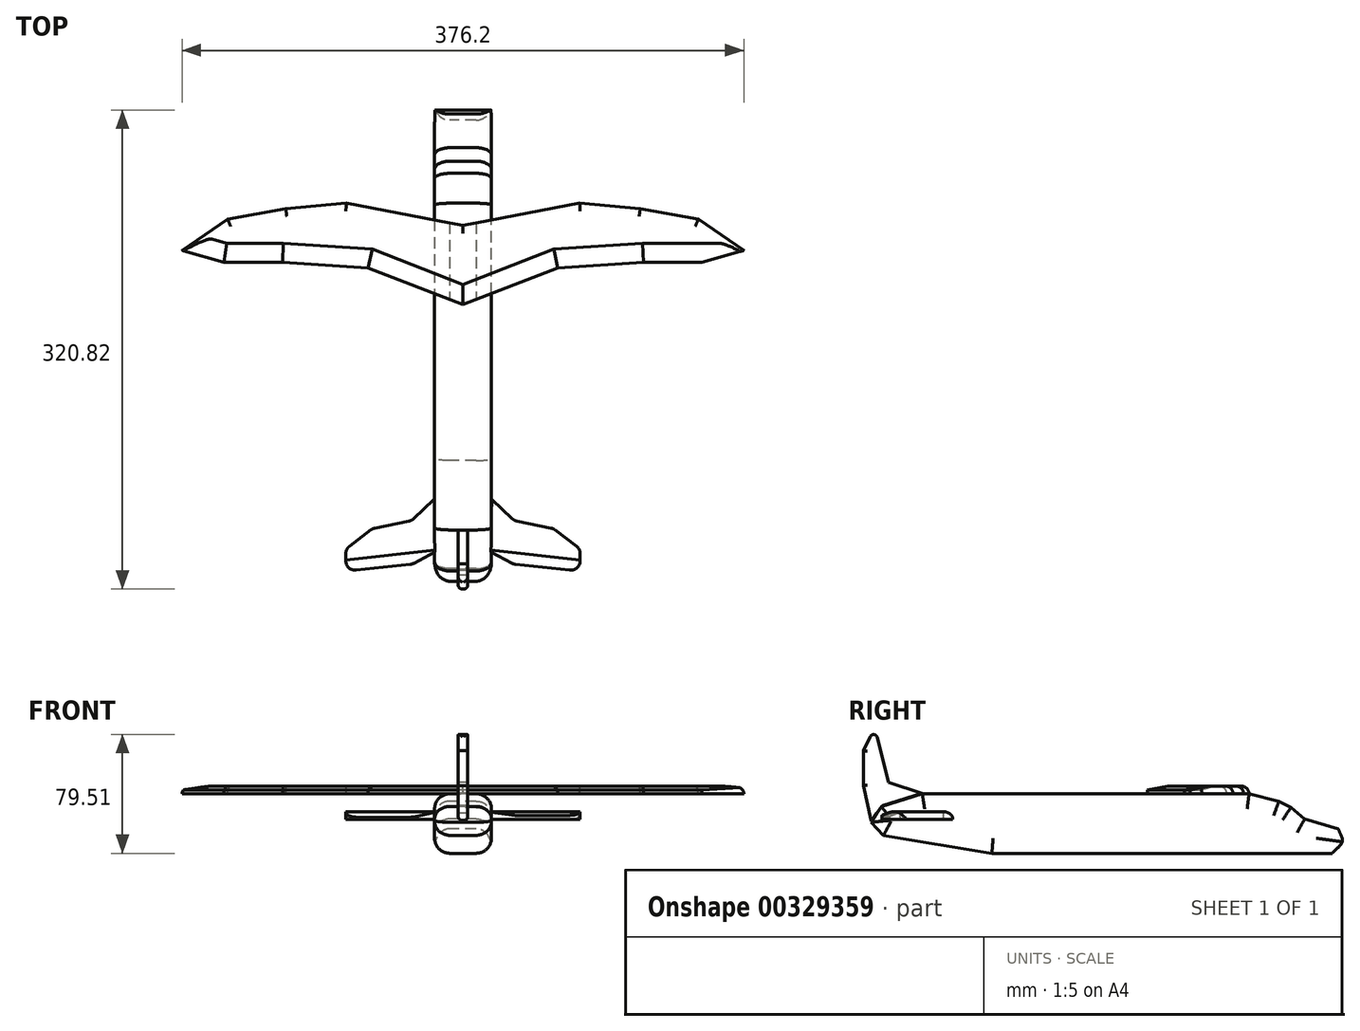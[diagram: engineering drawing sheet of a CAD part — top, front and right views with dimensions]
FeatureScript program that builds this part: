
annotation { "Feature Type Name" : "Feature", "Feature Type Description" : "" }
export const myFeature = defineFeature(function(context is Context, id is Id, definition is map)
    precondition{}
    {
        {
            var Q0;
            Q0=qCreatedBy(makeId("Right.planeOp"),FACE);
            var sketch = newSketch(context, id + "F0", { "sketchPlane" : qUnion([Q0])});
            skLineSegment(sketch, "E0", {"start": v(-78.46, 0) * mm, "end": v(149.41, 0) * mm});
            skLineSegment(sketch, "E1", {"start": v(149.41, 0) * mm, "end": v(157.23, 7.66) * mm});
            skLineSegment(sketch, "E2", {"start": v(157.23, 7.66) * mm, "end": v(153.48, 16.41) * mm});
            skLineSegment(sketch, "E3", {"start": v(153.48, 16.41) * mm, "end": v(130.97, 22.97) * mm});
            skLineSegment(sketch, "E4", {"start": v(130.97, 22.97) * mm, "end": v(121.9, 30.79) * mm});
            skLineSegment(sketch, "E5", {"start": v(121.9, 30.79) * mm, "end": v(113.78, 34.85) * mm});
            skLineSegment(sketch, "E6", {"start": v(113.78, 34.85) * mm, "end": v(93.77, 39.85) * mm});
            skLineSegment(sketch, "E7", {"start": v(93.77, 39.85) * mm, "end": v(-34.7, 39.85) * mm});
            skLineSegment(sketch, "E8", {"start": v(-34.7, 39.85) * mm, "end": v(-125.03, 39.85) * mm});
            skLineSegment(sketch, "E9", {"start": v(-125.03, 39.85) * mm, "end": v(-152.54, 31.41) * mm});
            skLineSegment(sketch, "E10", {"start": v(-152.54, 31.41) * mm, "end": v(-159.42, 20.79) * mm});
            skLineSegment(sketch, "E11", {"start": v(-159.42, 20.79) * mm, "end": v(-150.98, 12.03) * mm});
            skLineSegment(sketch, "E12", {"start": v(-150.98, 12.03) * mm, "end": v(-78.46, 0) * mm});
            skSolve(sketch);
        }
        {
            var Q0;
            Q0=qSketchRegion(id+"F0",true);
            extrude(context, id + "F1", {"entities" : qUnion([Q0]), "endBound" : BoundingType.SYMMETRIC, "depth" : 38.1 * mm});
        }
        {
            var Q0;
            Q0=makeQuery(id+"F1.opExtrude","CAP_FACE",FACE,{"disambiguationData":[OSD([sQuery(id+"F0.wireOp",EDGE,"E0"),sQuery(id+"F0.wireOp",EDGE,"E1"),sQuery(id+"F0.wireOp",EDGE,"E2"),sQuery(id+"F0.wireOp",EDGE,"E3"),sQuery(id+"F0.wireOp",EDGE,"E4"),sQuery(id+"F0.wireOp",EDGE,"E5"),sQuery(id+"F0.wireOp",EDGE,"E6"),sQuery(id+"F0.wireOp",EDGE,"E7"),sQuery(id+"F0.wireOp",EDGE,"E8"),sQuery(id+"F0.wireOp",EDGE,"E9"),sQuery(id+"F0.wireOp",EDGE,"E10"),sQuery(id+"F0.wireOp",EDGE,"E11"),sQuery(id+"F0.wireOp",EDGE,"E12")])],"isStart":false});
            var Q1;
            Q1=makeQuery(id+"F1.opExtrude","CAP_FACE",FACE,{"disambiguationData":[OSD([sQuery(id+"F0.wireOp",EDGE,"E0"),sQuery(id+"F0.wireOp",EDGE,"E1"),sQuery(id+"F0.wireOp",EDGE,"E2"),sQuery(id+"F0.wireOp",EDGE,"E3"),sQuery(id+"F0.wireOp",EDGE,"E4"),sQuery(id+"F0.wireOp",EDGE,"E5"),sQuery(id+"F0.wireOp",EDGE,"E6"),sQuery(id+"F0.wireOp",EDGE,"E7"),sQuery(id+"F0.wireOp",EDGE,"E8"),sQuery(id+"F0.wireOp",EDGE,"E9"),sQuery(id+"F0.wireOp",EDGE,"E10"),sQuery(id+"F0.wireOp",EDGE,"E11"),sQuery(id+"F0.wireOp",EDGE,"E12")])],"isStart":true});
            fillet(context, id + "F2", {"entities" : qUnion([Q0, Q1]), "radius" : 10.16 * mm, "tangentPropagation" : true, "allowEdgeOverflow" : false});
        }
        {
            var Q0;
            Q0=makeQuery(id+"F1.opExtrude","SWEPT_EDGE",EDGE,{"disambiguationData":[OSD([sQuery(id+"F0.wireOp",EDGE,"E1"),sQuery(id+"F0.wireOp",EDGE,"E2")])]});
            fillet(context, id + "F3", {"entities" : qUnion([Q0]), "radius" : 5.08 * mm, "tangentPropagation" : true, "allowEdgeOverflow" : false});
        }
        {
            var Q0;
            Q0=makeQuery(id+"F1.opExtrude","SWEPT_FACE",FACE,{"disambiguationData":[OSD([sQuery(id+"F0.wireOp",EDGE,"E7"),sQuery(id+"F0.wireOp",EDGE,"E8")])]});
            var sketch = newSketch(context, id + "F4", { "sketchPlane" : qUnion([Q0])});
            skLineSegment(sketch, "E13", {"start": v(0, 78.89) * mm, "end": v(-78.16, 93.77) * mm});
            skLineSegment(sketch, "E14", {"start": v(-78.16, 93.77) * mm, "end": v(-118.71, 90.18) * mm});
            skLineSegment(sketch, "E15", {"start": v(-118.71, 90.18) * mm, "end": v(-157.58, 83.07) * mm});
            skLineSegment(sketch, "E16", {"start": v(-157.58, 83.07) * mm, "end": v(-188.1, 62.17) * mm});
            skLineSegment(sketch, "E17", {"start": v(-188.1, 62.17) * mm, "end": v(-160.1, 54.23) * mm});
            skLineSegment(sketch, "E18", {"start": v(-160.1, 54.23) * mm, "end": v(-120.8, 54.23) * mm});
            skLineSegment(sketch, "E19", {"start": v(-120.8, 54.23) * mm, "end": v(-63.54, 50.47) * mm});
            skLineSegment(sketch, "E20", {"start": v(-63.54, 50.47) * mm, "end": v(0, 25.8) * mm});
            skLineSegment(sketch, "E21", {"start": v(0, 0) * mm, "end": v(0, 154.96) * mm, "construction": true});
            skLineSegment(sketch, "E22.0.MirrorCS", {"start": v(78.16, 93.77) * mm, "end": v(118.71, 90.18) * mm});
            skLineSegment(sketch, "E22.1.MirrorCS", {"start": v(118.71, 90.18) * mm, "end": v(157.58, 83.07) * mm});
            skLineSegment(sketch, "E22.2.MirrorCS", {"start": v(63.54, 50.47) * mm, "end": v(0, 25.8) * mm});
            skLineSegment(sketch, "E22.3.MirrorCS", {"start": v(157.58, 83.07) * mm, "end": v(188.1, 62.17) * mm});
            skLineSegment(sketch, "E22.4.MirrorCS", {"start": v(188.1, 62.17) * mm, "end": v(160.1, 54.23) * mm});
            skLineSegment(sketch, "E22.5.MirrorCS", {"start": v(160.1, 54.23) * mm, "end": v(120.8, 54.23) * mm});
            skLineSegment(sketch, "E22.6.MirrorCS", {"start": v(0, 78.89) * mm, "end": v(78.16, 93.77) * mm});
            skLineSegment(sketch, "E22.7.MirrorCS", {"start": v(120.8, 54.23) * mm, "end": v(63.54, 50.47) * mm});
            skSolve(sketch);
        }
        {
            var Q0;
            Q0=qSketchRegion(id+"F4",true);
            extrude(context, id + "F5", {"entities" : qUnion([Q0]), "operationType" : NewBodyOperationType.ADD, "depth" : 5.08 * mm});
        }
        {
            var Q0;
            Q0=qCreatedBy(makeId("Right.planeOp"),FACE);
            var sketch = newSketch(context, id + "F6", { "sketchPlane" : qUnion([Q0])});
            skLineSegment(sketch, "E23", {"start": v(-159.33, 21.94) * mm, "end": v(-164.55, 45.27) * mm});
            skLineSegment(sketch, "E24", {"start": v(-164.55, 45.27) * mm, "end": v(-164.55, 68.9) * mm});
            skLineSegment(sketch, "E25", {"start": v(-164.55, 68.9) * mm, "end": v(-156.87, 84.25) * mm});
            skLineSegment(sketch, "E26", {"start": v(-156.87, 84.25) * mm, "end": v(-147.67, 47.42) * mm});
            skLineSegment(sketch, "E27", {"start": v(-147.67, 47.42) * mm, "end": v(-125.26, 40.05) * mm});
            skLineSegment(sketch, "E28", {"start": v(-125.26, 40.05) * mm, "end": v(-151.66, 31.77) * mm});
            skLineSegment(sketch, "E29", {"start": v(-151.66, 31.77) * mm, "end": v(-159.33, 21.94) * mm});
            skSolve(sketch);
        }
        {
            var Q0;
            Q0=makeQuery(id+"F6.imprint","IMPRINT",FACE,{"disambiguationData":[TD([[makeQuery(id+"F6.imprint","IMPRINT",EDGE,{"derivedFrom":sQuery(id+"F6.wireOp",EDGE,"E23")}),-1.0]])]});
            extrude(context, id + "F7", {"entities" : qUnion([Q0]), "operationType" : NewBodyOperationType.ADD, "endBound" : BoundingType.SYMMETRIC, "depth" : 6.35 * mm});
        }
        {
            var Q0;
            Q0=makeQuery(id+"F7.opExtrude","CAP_EDGE",EDGE,{"disambiguationData":[OSD([sQuery(id+"F6.wireOp",EDGE,"E25")])],"isStart":false});
            var Q1;
            Q1=makeQuery(id+"F7.opExtrude","CAP_EDGE",EDGE,{"disambiguationData":[OSD([sQuery(id+"F6.wireOp",EDGE,"E24")])],"isStart":false});
            var Q2;
            Q2=makeQuery(id+"F7.opExtrude","CAP_EDGE",EDGE,{"disambiguationData":[OSD([sQuery(id+"F6.wireOp",EDGE,"E23")])],"isStart":false});
            var Q3;
            Q3=makeQuery(id+"F7.opExtrude","CAP_EDGE",EDGE,{"disambiguationData":[OSD([sQuery(id+"F6.wireOp",EDGE,"E23")])],"isStart":true});
            var Q4;
            Q4=makeQuery(id+"F7.opExtrude","CAP_EDGE",EDGE,{"disambiguationData":[OSD([sQuery(id+"F6.wireOp",EDGE,"E24")])],"isStart":true});
            var Q5;
            Q5=makeQuery(id+"F7.opExtrude","CAP_EDGE",EDGE,{"disambiguationData":[OSD([sQuery(id+"F6.wireOp",EDGE,"E25")])],"isStart":true});
            var Q6;
            Q6=makeQuery(id+"F7.opExtrude","SWEPT_EDGE",EDGE,{"disambiguationData":[OSD([sQuery(id+"F6.wireOp",EDGE,"E25"),sQuery(id+"F6.wireOp",EDGE,"E26")])]});
            fillet(context, id + "F8", {"entities" : qUnion([Q0, Q1, Q2, Q3, Q4, Q5, Q6]), "radius" : 2.54 * mm, "tangentPropagation" : true, "allowEdgeOverflow" : false});
        }
        {
            var Q0;
            Q0=qCreatedBy(makeId("Top.planeOp"),FACE);
            cPlane(context, id + "F9", {"entities" : qUnion([Q0]), "cplaneType" : CPlaneType.OFFSET, "offset" : 25.4 * mm, "width" : 152.4 * mm, "height" : 152.4 * mm});
        }
        {
            var Q0;
            Q0=qCreatedBy(id+"F9.planeOp",FACE);
            var sketch = newSketch(context, id + "F10", { "sketchPlane" : qUnion([Q0])});
            skLineSegment(sketch, "E30", {"start": v(19.38, -104.66) * mm, "end": v(33.06, -117.54) * mm});
            skLineSegment(sketch, "E31", {"start": v(36.15, -119.14) * mm, "end": v(58.99, -123.79) * mm});
            skLineSegment(sketch, "E32", {"start": v(61.55, -124.94) * mm, "end": v(75.97, -135.84) * mm});
            skLineSegment(sketch, "E33", {"start": v(78.49, -140.9) * mm, "end": v(78.49, -145.67) * mm});
            skLineSegment(sketch, "E34", {"start": v(71.45, -151.98) * mm, "end": v(35.17, -148.03) * mm});
            skLineSegment(sketch, "E35", {"start": v(32.84, -147.3) * mm, "end": v(17.61, -139.07) * mm});
            skLineSegment(sketch, "E36", {"start": v(19.38, -104.66) * mm, "end": v(17.61, -139.07) * mm});
            skPoint(sketch, "E37.visualSharp", {"position": v(78.49, -137.75) * mm});
            skArc(sketch, "E37.filletArc", {"start": v(78.49, -140.9) * mm, "mid": v(77.82, -138.08) * mm, "end": v(75.97, -135.84) * mm});
            skPoint(sketch, "E38.visualSharp", {"position": v(78.49, -152.74) * mm});
            skArc(sketch, "E38.filletArc", {"start": v(71.45, -151.98) * mm, "mid": v(76.38, -150.4) * mm, "end": v(78.49, -145.67) * mm});
            skPoint(sketch, "E39.visualSharp", {"position": v(60.4, -124.07) * mm});
            skArc(sketch, "E39.filletArc", {"start": v(61.55, -124.94) * mm, "mid": v(60.33, -124.22) * mm, "end": v(58.99, -123.79) * mm});
            skPoint(sketch, "E40.visualSharp", {"position": v(34.38, -118.78) * mm});
            skArc(sketch, "E40.filletArc", {"start": v(33.06, -117.54) * mm, "mid": v(34.5, -118.56) * mm, "end": v(36.15, -119.14) * mm});
            skPoint(sketch, "E41.visualSharp", {"position": v(33.93, -147.9) * mm});
            skArc(sketch, "E41.filletArc", {"start": v(32.84, -147.3) * mm, "mid": v(33.97, -147.78) * mm, "end": v(35.17, -148.03) * mm});
            skLineSegment(sketch, "E42", {"start": v(0, 0) * mm, "end": v(0, -233.9) * mm, "construction": true});
            skLineSegment(sketch, "E43.0.MirrorCS", {"start": v(-71.45, -151.98) * mm, "end": v(-35.17, -148.03) * mm});
            skLineSegment(sketch, "E44.0.MirrorCS", {"start": v(-78.49, -140.9) * mm, "end": v(-78.49, -145.67) * mm});
            skArc(sketch, "E44.1.MirrorCS", {"start": v(-78.49, -140.9) * mm, "mid": v(-77.82, -138.08) * mm, "end": v(-75.97, -135.84) * mm});
            skArc(sketch, "E44.2.MirrorCS", {"start": v(-61.55, -124.94) * mm, "mid": v(-60.33, -124.22) * mm, "end": v(-58.99, -123.79) * mm});
            skArc(sketch, "E44.3.MirrorCS", {"start": v(-32.84, -147.3) * mm, "mid": v(-33.97, -147.78) * mm, "end": v(-35.17, -148.03) * mm});
            skArc(sketch, "E44.4.MirrorCS", {"start": v(-33.06, -117.54) * mm, "mid": v(-34.5, -118.56) * mm, "end": v(-36.15, -119.14) * mm});
            skArc(sketch, "E44.5.MirrorCS", {"start": v(-71.45, -151.98) * mm, "mid": v(-76.38, -150.4) * mm, "end": v(-78.49, -145.67) * mm});
            skLineSegment(sketch, "E44.7.MirrorCS", {"start": v(-19.38, -104.66) * mm, "end": v(-17.61, -139.07) * mm});
            skPoint(sketch, "E44.8.MirrorP", {"position": v(-60.4, -124.07) * mm});
            skPoint(sketch, "E44.9.MirrorP", {"position": v(-78.49, -137.75) * mm});
            skLineSegment(sketch, "E44.10.MirrorCS", {"start": v(-32.84, -147.3) * mm, "end": v(-17.61, -139.07) * mm});
            skPoint(sketch, "E44.11.MirrorP", {"position": v(-33.93, -147.9) * mm});
            skPoint(sketch, "E44.12.MirrorP", {"position": v(-78.49, -152.74) * mm});
            skLineSegment(sketch, "E44.13.MirrorCS", {"start": v(-61.55, -124.94) * mm, "end": v(-75.97, -135.84) * mm});
            skPoint(sketch, "E44.14.MirrorP", {"position": v(-34.38, -118.78) * mm});
            skLineSegment(sketch, "E44.15.MirrorCS", {"start": v(-19.38, -104.66) * mm, "end": v(-33.06, -117.54) * mm});
            skLineSegment(sketch, "E44.16.MirrorCS", {"start": v(-36.15, -119.14) * mm, "end": v(-58.99, -123.79) * mm});
            skSolve(sketch);
        }
        {
            var Q0;
            Q0=makeQuery(id+"F10.imprint","IMPRINT",FACE,{"disambiguationData":[TD([[makeQuery(id+"F10.imprint","IMPRINT",EDGE,{"derivedFrom":sQuery(id+"F10.wireOp",EDGE,"E30")}),-1.0]])]});
            var Q1;
            Q1=makeQuery(id+"F10.imprint","IMPRINT",FACE,{"disambiguationData":[TD([[makeQuery(id+"F10.imprint","IMPRINT",EDGE,{"derivedFrom":sQuery(id+"F10.wireOp",EDGE,"E44.0.MirrorCS")}),1.0]])]});
            extrude(context, id + "F11", {"entities" : qUnion([Q0, Q1]), "operationType" : NewBodyOperationType.ADD, "endBound" : BoundingType.SYMMETRIC, "depth" : 5.08 * mm});
        }
        {
            var Q0;
            Q0=makeQuery(id+"F5.opExtrude","CAP_EDGE",EDGE,{"disambiguationData":[OSD([sQuery(id+"F4.wireOp",EDGE,"E13")])],"isStart":false});
            var Q1;
            Q1=makeQuery(id+"F5.opExtrude","CAP_EDGE",EDGE,{"disambiguationData":[OSD([sQuery(id+"F4.wireOp",EDGE,"E22.6.MirrorCS")])],"isStart":false});
            var Q2;
            Q2=makeQuery(id+"F5.opExtrude","CAP_EDGE",EDGE,{"disambiguationData":[OSD([sQuery(id+"F4.wireOp",EDGE,"E22.1.MirrorCS")])],"isStart":false});
            var Q3;
            Q3=makeQuery(id+"F5.opExtrude","CAP_EDGE",EDGE,{"disambiguationData":[OSD([sQuery(id+"F4.wireOp",EDGE,"E22.0.MirrorCS")])],"isStart":false});
            var Q4;
            Q4=makeQuery(id+"F5.opExtrude","CAP_EDGE",EDGE,{"disambiguationData":[OSD([sQuery(id+"F4.wireOp",EDGE,"E14")])],"isStart":false});
            var Q5;
            Q5=makeQuery(id+"F5.opExtrude","CAP_EDGE",EDGE,{"disambiguationData":[OSD([sQuery(id+"F4.wireOp",EDGE,"E15")])],"isStart":false});
            var Q6;
            Q6=makeQuery(id+"F5.opExtrude","CAP_EDGE",EDGE,{"disambiguationData":[OSD([sQuery(id+"F4.wireOp",EDGE,"E16")])],"isStart":false});
            var Q7;
            Q7=makeQuery(id+"F5.opExtrude","CAP_EDGE",EDGE,{"disambiguationData":[OSD([sQuery(id+"F4.wireOp",EDGE,"E22.3.MirrorCS")])],"isStart":false});
            var Q8;
            Q8=makeQuery(id+"F11.opExtrude","CAP_EDGE",EDGE,{"disambiguationData":[OSD([sQuery(id+"F10.wireOp",EDGE,"E30")])],"isStart":false});
            var Q9;
            Q9=makeQuery(id+"F11.opExtrude","CAP_EDGE",EDGE,{"disambiguationData":[OSD([sQuery(id+"F10.wireOp",EDGE,"E44.15.MirrorCS")])],"isStart":false});
            var Q10;
            Q10=makeQuery(id+"F11.opExtrude","CAP_EDGE",EDGE,{"disambiguationData":[OSD([sQuery(id+"F10.wireOp",EDGE,"E40.filletArc")])],"isStart":false});
            var Q11;
            Q11=makeQuery(id+"F11.opExtrude","CAP_EDGE",EDGE,{"disambiguationData":[OSD([sQuery(id+"F10.wireOp",EDGE,"E31")])],"isStart":false});
            var Q12;
            Q12=makeQuery(id+"F11.opExtrude","CAP_EDGE",EDGE,{"disambiguationData":[OSD([sQuery(id+"F10.wireOp",EDGE,"E39.filletArc")])],"isStart":false});
            var Q13;
            Q13=makeQuery(id+"F11.opExtrude","CAP_EDGE",EDGE,{"disambiguationData":[OSD([sQuery(id+"F10.wireOp",EDGE,"E32")])],"isStart":false});
            var Q14;
            Q14=makeQuery(id+"F11.opExtrude","CAP_EDGE",EDGE,{"disambiguationData":[OSD([sQuery(id+"F10.wireOp",EDGE,"E37.filletArc")])],"isStart":false});
            var Q15;
            Q15=makeQuery(id+"F11.opExtrude","CAP_EDGE",EDGE,{"disambiguationData":[OSD([sQuery(id+"F10.wireOp",EDGE,"E44.4.MirrorCS")])],"isStart":false});
            var Q16;
            Q16=makeQuery(id+"F11.opExtrude","CAP_EDGE",EDGE,{"disambiguationData":[OSD([sQuery(id+"F10.wireOp",EDGE,"E44.16.MirrorCS")])],"isStart":false});
            var Q17;
            Q17=makeQuery(id+"F11.opExtrude","SWEPT_EDGE",EDGE,{"disambiguationData":[OSD([sQuery(id+"F10.wireOp",EDGE,"E44.2.MirrorCS"),sQuery(id+"F10.wireOp",EDGE,"E44.13.MirrorCS")])]});
            var Q18;
            Q18=makeQuery(id+"F11.opExtrude","CAP_EDGE",EDGE,{"disambiguationData":[OSD([sQuery(id+"F10.wireOp",EDGE,"E44.13.MirrorCS")])],"isStart":false});
            fillet(context, id + "F12", {"entities" : qUnion([Q0, Q1, Q2, Q3, Q4, Q5, Q6, Q7, Q8, Q9, Q10, Q11, Q12, Q13, Q14, Q15, Q16, Q17, Q18]), "radius" : 5.08 * mm, "allowEdgeOverflow" : false});
        }
        {
            var Q0;
            Q0=makeQuery(id+"F5.opExtrude","CAP_EDGE",EDGE,{"disambiguationData":[OSD([sQuery(id+"F4.wireOp",EDGE,"E22.5.MirrorCS")])],"isStart":false});
            var Q1;
            Q1=makeQuery(id+"F5.opExtrude","CAP_EDGE",EDGE,{"disambiguationData":[OSD([sQuery(id+"F4.wireOp",EDGE,"E22.7.MirrorCS")])],"isStart":false});
            var Q2;
            Q2=makeQuery(id+"F5.opExtrude","CAP_EDGE",EDGE,{"disambiguationData":[OSD([sQuery(id+"F4.wireOp",EDGE,"E22.2.MirrorCS")])],"isStart":false});
            var Q3;
            Q3=makeQuery(id+"F5.opExtrude","CAP_EDGE",EDGE,{"disambiguationData":[OSD([sQuery(id+"F4.wireOp",EDGE,"E20")])],"isStart":false});
            var Q4;
            Q4=makeQuery(id+"F5.opExtrude","CAP_EDGE",EDGE,{"disambiguationData":[OSD([sQuery(id+"F4.wireOp",EDGE,"E19")])],"isStart":false});
            var Q5;
            Q5=makeQuery(id+"F5.opExtrude","CAP_EDGE",EDGE,{"disambiguationData":[OSD([sQuery(id+"F4.wireOp",EDGE,"E18")])],"isStart":false});
            var Q6;
            Q6=makeQuery(id+"F5.opExtrude","CAP_EDGE",EDGE,{"disambiguationData":[OSD([sQuery(id+"F4.wireOp",EDGE,"E17")])],"isStart":false});
            chamfer(context, id + "F13", {"entities" : qUnion([Q0, Q1, Q2, Q3, Q4, Q5, Q6]), "chamferType" : ChamferType.TWO_OFFSETS, "width1" : 2.54 * mm, "oppositeDirection" : false, "width2" : 12.7 * mm});
        }
        {
            var Q0;
            Q0=makeQuery(id+"F11.opExtrude","CAP_EDGE",EDGE,{"disambiguationData":[OSD([sQuery(id+"F10.wireOp",EDGE,"E43.0.MirrorCS")])],"isStart":false});
            chamfer(context, id + "F14", {"entities" : qUnion([Q0]), "chamferType" : ChamferType.TWO_OFFSETS, "width1" : 7.62 * mm, "oppositeDirection" : false, "width2" : 3.8 * mm});
        }
        {
            var Q0;
            Q0=makeQuery(id+"F11.opExtrude","CAP_EDGE",EDGE,{"disambiguationData":[OSD([sQuery(id+"F10.wireOp",EDGE,"E34")])],"isStart":false});
            chamfer(context, id + "F15", {"entities" : qUnion([Q0]), "chamferType" : ChamferType.TWO_OFFSETS, "width1" : 2.54 * mm, "oppositeDirection" : false, "width2" : 7.62 * mm});
        }
    });
